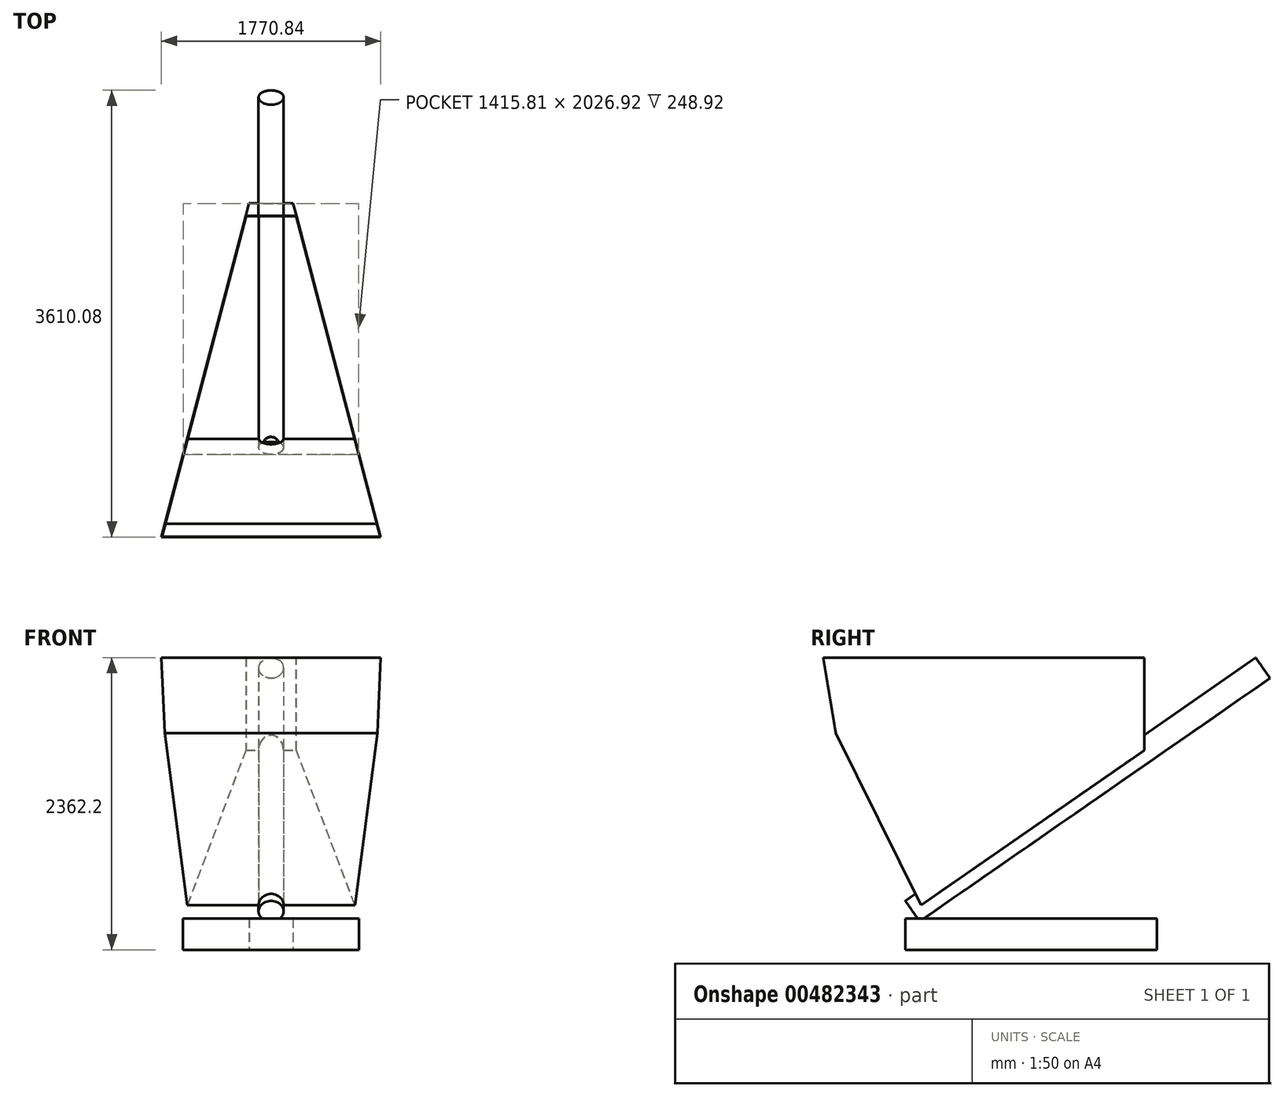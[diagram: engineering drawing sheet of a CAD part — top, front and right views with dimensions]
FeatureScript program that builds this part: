
annotation { "Feature Type Name" : "Feature", "Feature Type Description" : "" }
export const myFeature = defineFeature(function(context is Context, id is Id, definition is map)
    precondition{}
    {
        {
            var Q0;
            Q0=qCreatedBy(makeId("Top.planeOp"),FACE);
            var sketch = newSketch(context, id + "F0", { "sketchPlane" : qUnion([Q0])});
            skLineSegment(sketch, "E0", {"start": v(-177.8, 0) * mm, "end": v(177.8, 0) * mm});
            skLineSegment(sketch, "E1", {"start": v(177.8, 0) * mm, "end": v(711.2, -2032) * mm});
            skLineSegment(sketch, "E2", {"start": v(711.2, -2032) * mm, "end": v(-711.2, -2032) * mm});
            skLineSegment(sketch, "E3", {"start": v(-711.2, -2032) * mm, "end": v(-177.8, 0) * mm});
            skSolve(sketch);
        }
        {
            var Q0;
            Q0 = qSketchRegion(id + "F0", true);
            extrude(context, id + "F1", {"entities" : qUnion([Q0]), "depth" : 254 * mm, "offsetDistance" : 25.4 * mm});
        }
        {
            var Q0;
            Q0=qCreatedBy(makeId("Right.planeOp"),FACE);
            var sketch = newSketch(context, id + "F2", { "sketchPlane" : qUnion([Q0])});
            skLineSegment(sketch, "E4", {"start": v(-2057.55, 254) * mm, "end": v(877.06, 2293.04) * mm, "construction": true});
            skLineSegment(sketch, "E5", {"start": v(856.43, 2278.7) * mm, "end": v(-1974.03, 312.04) * mm});
            skLineSegment(sketch, "E6", {"start": v(-1974.03, 312.04) * mm, "end": v(-2032, 395.47) * mm});
            skLineSegment(sketch, "E7", {"start": v(-2032, 395.47) * mm, "end": v(798.45, 2362.14) * mm});
            skLineSegment(sketch, "E8", {"start": v(798.45, 2362.14) * mm, "end": v(856.43, 2278.7) * mm});
            skLineSegment(sketch, "E9", {"start": v(0, 1683.64) * mm, "end": v(57.97, 1600.2) * mm, "construction": true});
            skLineSegment(sketch, "E10", {"start": v(856.43, 2278.7) * mm, "end": v(914.4, 2195.27) * mm, "construction": true});
            skLineSegment(sketch, "E11", {"start": v(-1974.03, 312.04) * mm, "end": v(-1916.05, 228.6) * mm, "construction": true});
            skSolve(sketch);
        }
        {
            var Q0;
            Q0 = qSketchRegion(id + "F2", true);
            var Q1;
            Q1=sQuery(id+"F2.wireOp",EDGE,"E4");
            revolve(context, id + "F3", {"operationType" : NewBodyOperationType.ADD, "entities" : qUnion([Q0]), "axis" : qUnion([Q1]), "revolveType" : RevolveType.FULL});
        }
        {
            var Q0;
            Q0=qCreatedBy(makeId("Right.planeOp"),FACE);
            var sketch = newSketch(context, id + "F4", { "sketchPlane" : qUnion([Q0])});
            skLineSegment(sketch, "E12", {"start": v(-101.6, 1613.04) * mm, "end": v(-1905, 360) * mm});
            skLineSegment(sketch, "E13", {"start": v(-1905, 360) * mm, "end": v(-2592.9, 1752.6) * mm});
            skLineSegment(sketch, "E14", {"start": v(-2592.9, 1752.6) * mm, "end": v(-2695.68, 2362.2) * mm});
            skLineSegment(sketch, "E15", {"start": v(-2695.68, 2362.2) * mm, "end": v(-101.6, 2362.2) * mm});
            skLineSegment(sketch, "E16", {"start": v(-101.6, 2362.2) * mm, "end": v(-101.6, 1613.04) * mm});
            skSolve(sketch);
        }
        {
            var Q0;
            Q0 = qSketchRegion(id + "F4", true);
            var Q1;
            Q1=makeQuery(id+"F1.opExtrude","SWEPT_FACE",FACE,{"disambiguationData":[OSD([sQuery(id+"F0.wireOp",EDGE,"E3")])]});
            var Q2;
            Q2=makeQuery(id+"F1.opExtrude","SWEPT_FACE",FACE,{"disambiguationData":[OSD([sQuery(id+"F0.wireOp",EDGE,"E1")])]});
            extrude(context, id + "F5", {"entities" : qUnion([Q0]), "operationType" : NewBodyOperationType.ADD, "endBound" : BoundingType.UP_TO_SURFACE, "oppositeDirection" : true, "depth" : 25.4 * mm, "endBoundEntityFace" : qUnion([Q1]), "offsetDistance" : 25.4 * mm, "hasSecondDirection" : true, "secondDirectionBound" : BoundingType.UP_TO_SURFACE, "secondDirectionOppositeDirection" : false, "secondDirectionDepth" : 25.4 * mm, "secondDirectionBoundEntityFace" : qUnion([Q2])});
        }
        {
            var Q0;
            Q0=makeQuery(id+"F5.opExtrude","SWEPT_FACE",FACE,{"disambiguationData":[OSD([sQuery(id+"F4.wireOp",EDGE,"E15")])]});
            shell(context, id + "F6", {"entities" : qUnion([Q0]), "thickness" : 2.54 * mm});
        }
    });
